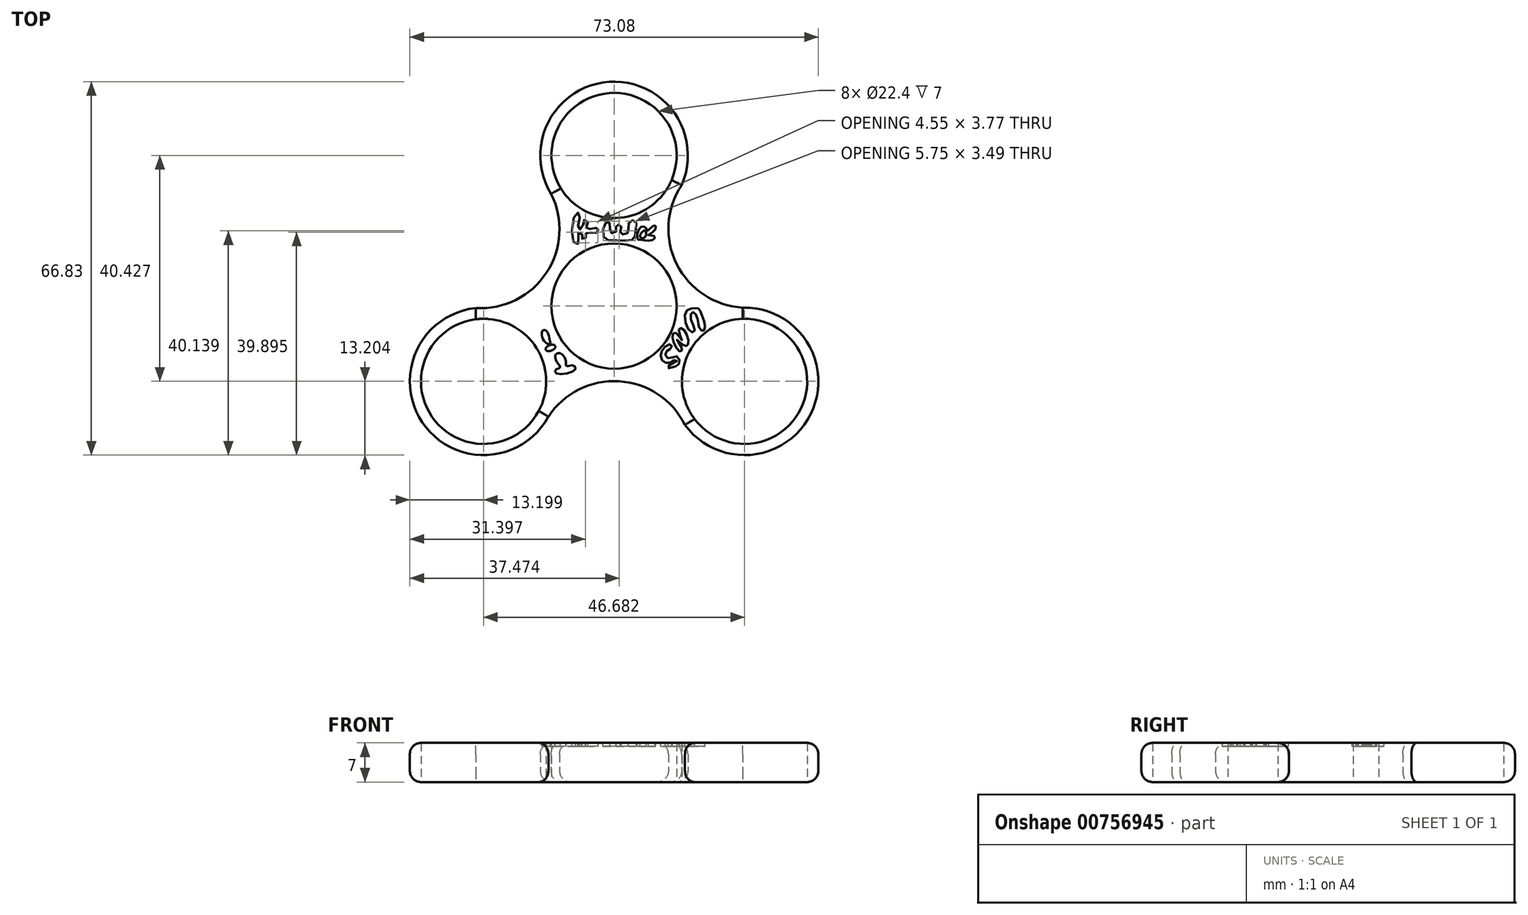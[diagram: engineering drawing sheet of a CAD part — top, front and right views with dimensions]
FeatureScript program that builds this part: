
annotation { "Feature Type Name" : "Feature", "Feature Type Description" : "" }
export const myFeature = defineFeature(function(context is Context, id is Id, definition is map)
    precondition{}
    {
        {
            var Q0;
            Q0=qCreatedBy(makeId("Top.planeOp"),FACE);
            var sketch = newSketch(context, id + "F0", { "sketchPlane" : qUnion([Q0])});
            skCircle(sketch, "E0", {"center": v(0, 0) * mm, "radius": 11.2 * mm});
            skCircle(sketch, "E1", {"center": v(0, 26.95) * mm, "radius": 11.2 * mm});
            skArc(sketch, "E2", {"start": v(10.96, 19.6) * mm, "mid": v(0.3, 40.15) * mm, "end": v(-11.27, 20.08) * mm});
            skArc(sketch, "E3.1.0", {"start": v(-22.44, -0.3) * mm, "mid": v(-34.92, -19.82) * mm, "end": v(-11.76, -19.8) * mm});
            skCircle(sketch, "E3.1.1", {"center": v(-23.34, -13.48) * mm, "radius": 11.2 * mm});
            skArc(sketch, "E3.2.0", {"start": v(11.49, -19.28) * mm, "mid": v(34.62, -20.33) * mm, "end": v(23.03, -0.28) * mm});
            skCircle(sketch, "E3.2.1", {"center": v(23.34, -13.48) * mm, "radius": 11.2 * mm});
            skArc(sketch, "E4", {"start": v(12.08, 21.62) * mm, "mid": v(11.21, 7.5) * mm, "end": v(23.03, -0.28) * mm});
            skArc(sketch, "E5.1.0", {"start": v(-24.76, -0.35) * mm, "mid": v(-12.1, 5.96) * mm, "end": v(-11.27, 20.08) * mm});
            skArc(sketch, "E5.2.0", {"start": v(12.69, -21.27) * mm, "mid": v(0.89, -13.46) * mm, "end": v(-11.76, -19.8) * mm});
            skSolve(sketch);
        }
        {
            var Q0;
            Q0=makeQuery(id+"F0.imprint","IMPRINT",FACE,{"disambiguationData":[TD([[makeQuery(id+"F0.imprint","IMPRINT",EDGE,{"derivedFrom":sQuery(id+"F0.wireOp",EDGE,"E0")}),-1.0]])]});
            extrude(context, id + "F1", {"entities" : qUnion([Q0]), "depth" : 7 * mm, "offsetDistance" : 25 * mm});
        }
        {
            var Q0;
            Q0=makeQuery(id+"F1.opExtrude","CAP_EDGE",EDGE,{"disambiguationData":[OSD([sQuery(id+"F0.wireOp",EDGE,"E5.2.0")])],"isStart":false});
            var Q1;
            Q1=makeQuery(id+"F1.opExtrude","CAP_EDGE",EDGE,{"disambiguationData":[OSD([sQuery(id+"F0.wireOp",EDGE,"E3.1.0")])],"isStart":false});
            var Q2;
            Q2=makeQuery(id+"F1.opExtrude","CAP_EDGE",EDGE,{"disambiguationData":[OSD([sQuery(id+"F0.wireOp",EDGE,"E5.1.0")])],"isStart":false});
            var Q3;
            Q3=makeQuery(id+"F1.opExtrude","CAP_EDGE",EDGE,{"disambiguationData":[OSD([sQuery(id+"F0.wireOp",EDGE,"E2")])],"isStart":false});
            var Q4;
            Q4=makeQuery(id+"F1.opExtrude","CAP_EDGE",EDGE,{"disambiguationData":[OSD([sQuery(id+"F0.wireOp",EDGE,"E4")])],"isStart":false});
            var Q5;
            Q5=makeQuery(id+"F1.opExtrude","CAP_EDGE",EDGE,{"disambiguationData":[OSD([sQuery(id+"F0.wireOp",EDGE,"E3.2.0")])],"isStart":false});
            fillet(context, id + "F2", {"entities" : qUnion([Q0, Q1, Q2, Q3, Q4, Q5]), "radius" : 2 * mm, "tangentPropagation" : true, "allowEdgeOverflow" : false});
        }
        {
            var Q0;
            Q0=makeQuery(id+"F1.opExtrude","CAP_EDGE",EDGE,{"disambiguationData":[OSD([sQuery(id+"F0.wireOp",EDGE,"E3.1.0")])],"isStart":true});
            var Q1;
            Q1=makeQuery(id+"F1.opExtrude","CAP_EDGE",EDGE,{"disambiguationData":[OSD([sQuery(id+"F0.wireOp",EDGE,"E5.1.0")])],"isStart":true});
            var Q2;
            Q2=makeQuery(id+"F1.opExtrude","CAP_EDGE",EDGE,{"disambiguationData":[OSD([sQuery(id+"F0.wireOp",EDGE,"E2")])],"isStart":true});
            var Q3;
            Q3=makeQuery(id+"F1.opExtrude","CAP_EDGE",EDGE,{"disambiguationData":[OSD([sQuery(id+"F0.wireOp",EDGE,"E4")])],"isStart":true});
            var Q4;
            Q4=makeQuery(id+"F1.opExtrude","CAP_EDGE",EDGE,{"disambiguationData":[OSD([sQuery(id+"F0.wireOp",EDGE,"E3.2.0")])],"isStart":true});
            fillet(context, id + "F3", {"entities" : qUnion([Q0, Q1, Q2, Q3, Q4]), "radius" : 2 * mm, "tangentPropagation" : true, "allowEdgeOverflow" : false});
        }
        {
            var Q0;
            Q0=makeQuery(id+"F1.opExtrude","CAP_FACE",FACE,{"disambiguationData":[OSD([sQuery(id+"F0.wireOp",EDGE,"E0"),sQuery(id+"F0.wireOp",EDGE,"E1"),sQuery(id+"F0.wireOp",EDGE,"E2"),sQuery(id+"F0.wireOp",EDGE,"E3.1.0"),sQuery(id+"F0.wireOp",EDGE,"E3.1.1"),sQuery(id+"F0.wireOp",EDGE,"E3.2.0"),sQuery(id+"F0.wireOp",EDGE,"E3.2.1"),sQuery(id+"F0.wireOp",EDGE,"E4"),sQuery(id+"F0.wireOp",EDGE,"E5.1.0"),sQuery(id+"F0.wireOp",EDGE,"E5.2.0")])],"isStart":false});
            var sketch = newSketch(context, id + "F4", { "sketchPlane" : qUnion([Q0])});
            skFitSpline(sketch, "E6", {"points": [v(16.26, -3.68) * mm, v(15.48, -1.06) * mm, v(15.06, -0.44) * mm, v(14.32, -0.4) * mm, v(12.83, -1.03) * mm, v(13.6, -4.54) * mm, v(14.4, -4.42) * mm, v(13.65, -1.93) * mm, v(14.16, -1.08) * mm, v(14.96, -2.37) * mm, v(15.16, -3.71) * mm, v(15.86, -4.48) * mm, v(16.26, -3.68) * mm]});
            skFitSpline(sketch, "E7", {"points": [v(13.24, -6.84) * mm, v(12.45, -4.22) * mm, v(11.6, -4.13) * mm, v(12.16, -6.17) * mm, v(11.04, -4.8) * mm, v(10.45, -5.32) * mm, v(11.7, -8.1) * mm, v(12.18, -7.72) * mm, v(11.25, -6.05) * mm, v(12.54, -7.07) * mm, v(13.24, -6.84) * mm]});
            skFitSpline(sketch, "E8", {"points": [v(10.4, -11) * mm, v(11.11, -10.76) * mm, v(11.7, -10.03) * mm, v(11.23, -8.98) * mm, v(9.89, -9.33) * mm, v(9.2, -8.89) * mm, v(9.59, -7.87) * mm, v(10.27, -7.51) * mm, v(10.16, -6.86) * mm, v(8.92, -7.48) * mm, v(8.36, -8.72) * mm, v(8.8, -9.92) * mm, v(9.98, -10.17) * mm, v(11, -9.65) * mm, v(11.22, -9.87) * mm, v(9.9, -10.51) * mm, v(9.74, -11.1) * mm, v(10.4, -11) * mm]});
            skFitSpline(sketch, "E9", {"points": [v(-8.52, -10.76) * mm, v(-8.63, -9.94) * mm, v(-9.39, -8.58) * mm, v(-10.37, -8.58) * mm, v(-10.38, -9.8) * mm, v(-9.66, -11.02) * mm, v(-10.44, -11.35) * mm, v(-10.38, -12.05) * mm, v(-6.95, -11.35) * mm, v(-7.39, -10.58) * mm, v(-8.52, -10.76) * mm]});
            skFitSpline(sketch, "E10", {"points": [v(-11.45, -6.3) * mm, v(-12.15, -4.42) * mm, v(-12.87, -4.5) * mm, v(-12.26, -6.56) * mm, v(-11.48, -6.7) * mm, v(-11.45, -6.3) * mm]});
            skFitSpline(sketch, "E11", {"points": [v(-10.94, -7.86) * mm, v(-10.51, -7.33) * mm, v(-10.88, -6.9) * mm, v(-12.17, -7.44) * mm, v(-12.06, -8.01) * mm, v(-10.94, -7.86) * mm]});
            skFitSpline(sketch, "E12", {"points": [v(-5.09, 13.03) * mm, v(-3.56, 13.1) * mm, v(-3, 13.17) * mm, v(-2.9, 13.9) * mm, v(-3.51, 13.96) * mm, v(-5.01, 13.88) * mm, v(-4.72, 15.07) * mm, v(-5.38, 15.4) * mm, v(-5.75, 13.87) * mm, v(-6.41, 13.9) * mm, v(-6.15, 16.38) * mm, v(-6.84, 16.6) * mm, v(-7.15, 11.23) * mm, v(-6.3, 11.37) * mm, v(-6.44, 13.08) * mm, v(-5.75, 12.92) * mm, v(-5.75, 12.1) * mm, v(-5.1, 12.13) * mm, v(-5.09, 13.03) * mm]});
            skFitSpline(sketch, "E13", {"points": [v(-0.77, 14.9) * mm, v(-1.42, 15) * mm, v(-1.84, 12.26) * mm, v(0.56, 11.75) * mm, v(3.34, 11.87) * mm, v(3.8, 13.06) * mm, v(3.8, 15.2) * mm, v(2.74, 15.08) * mm, v(2.56, 13.42) * mm, v(2.12, 12.9) * mm, v(1.14, 13) * mm, v(1.3, 14.14) * mm, v(0.83, 14.56) * mm, v(0.37, 14.3) * mm, v(0.33, 13.26) * mm, v(-0.64, 13.15) * mm, v(-0.77, 14.9) * mm]});
            skFitSpline(sketch, "E14", {"points": [v(4.78, 11.86) * mm, v(6.99, 11.85) * mm, v(7.2, 12.51) * mm, v(6.1, 12.7) * mm, v(7.3, 13.62) * mm, v(7.25, 14.44) * mm, v(5.92, 13.44) * mm, v(5.77, 13.9) * mm, v(4.76, 14.14) * mm, v(4.17, 12.03) * mm, v(4.78, 11.86) * mm]});
            skFitSpline(sketch, "E15", {"points": [v(4.66, 12.4) * mm, v(5.55, 12.35) * mm, v(5.46, 13.5) * mm, v(4.66, 12.4) * mm]});
            skSolve(sketch);
        }
        {
            var Q0;
            Q0=makeQuery(id+"F4.imprint","IMPRINT",FACE,{"disambiguationData":[TD([[makeQuery(id+"F4.imprint","IMPRINT",EDGE,{"derivedFrom":sQuery(id+"F4.wireOp",EDGE,"E6")}),1.0]])]});
            var Q1;
            Q1=makeQuery(id+"F4.imprint","IMPRINT",FACE,{"disambiguationData":[TD([[makeQuery(id+"F4.imprint","IMPRINT",EDGE,{"derivedFrom":sQuery(id+"F4.wireOp",EDGE,"E7")}),1.0]])]});
            var Q2;
            Q2=makeQuery(id+"F4.imprint","IMPRINT",FACE,{"disambiguationData":[TD([[makeQuery(id+"F4.imprint","IMPRINT",EDGE,{"derivedFrom":sQuery(id+"F4.wireOp",EDGE,"E8")}),1.0]])]});
            var Q3;
            Q3=makeQuery(id+"F4.imprint","IMPRINT",FACE,{"disambiguationData":[TD([[makeQuery(id+"F4.imprint","IMPRINT",EDGE,{"derivedFrom":sQuery(id+"F4.wireOp",EDGE,"E9")}),1.0]])]});
            var Q4;
            Q4=makeQuery(id+"F4.imprint","IMPRINT",FACE,{"disambiguationData":[TD([[makeQuery(id+"F4.imprint","IMPRINT",EDGE,{"derivedFrom":sQuery(id+"F4.wireOp",EDGE,"E10")}),1.0]])]});
            var Q5;
            Q5=makeQuery(id+"F4.imprint","IMPRINT",FACE,{"disambiguationData":[TD([[makeQuery(id+"F4.imprint","IMPRINT",EDGE,{"derivedFrom":sQuery(id+"F4.wireOp",EDGE,"E11")}),1.0]])]});
            var Q6;
            Q6=makeQuery(id+"F4.imprint","IMPRINT",FACE,{"disambiguationData":[TD([[makeQuery(id+"F4.imprint","IMPRINT",EDGE,{"derivedFrom":sQuery(id+"F4.wireOp",EDGE,"E14")}),1.0]])]});
            var Q7;
            Q7=makeQuery(id+"F4.imprint","IMPRINT",FACE,{"disambiguationData":[TD([[makeQuery(id+"F4.imprint","IMPRINT",EDGE,{"derivedFrom":sQuery(id+"F4.wireOp",EDGE,"E13")}),1.0]])]});
            var Q8;
            Q8=makeQuery(id+"F4.imprint","IMPRINT",FACE,{"disambiguationData":[TD([[makeQuery(id+"F4.imprint","IMPRINT",EDGE,{"derivedFrom":sQuery(id+"F4.wireOp",EDGE,"E12")}),1.0]])]});
            extrude(context, id + "F5", {"entities" : qUnion([Q0, Q1, Q2, Q3, Q4, Q5, Q6, Q7, Q8]), "operationType" : NewBodyOperationType.REMOVE, "oppositeDirection" : true, "depth" : 0.6 * mm, "offsetDistance" : 25 * mm});
        }
    });
